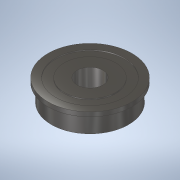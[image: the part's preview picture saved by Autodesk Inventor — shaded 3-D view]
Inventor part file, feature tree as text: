
AUTODESK INVENTOR PART (.ipt)
format: ipt  version: 2022.3 (Build 263350000, 350)  size: 220,160 bytes
history: native  units: in
note: dims shown in document units (in); Inventor stores cm internally (conversion verified against a paired STEP export)
features: revolve x1
ambient origin geometry x8: Origin, YZ Plane, XZ Plane, XY Plane, X Axis, Y Axis, Z Axis, Center Point
bodies: Solid1 (feature_tree)
feature tree (1):
  revolve  "Revolve1"  [1 undecoded]
note: 1 required parameter value undecoded (feature->parameter linkage not recoverable at this tier; creation-order binding heuristic only, values carry confidence <= 0.55)
